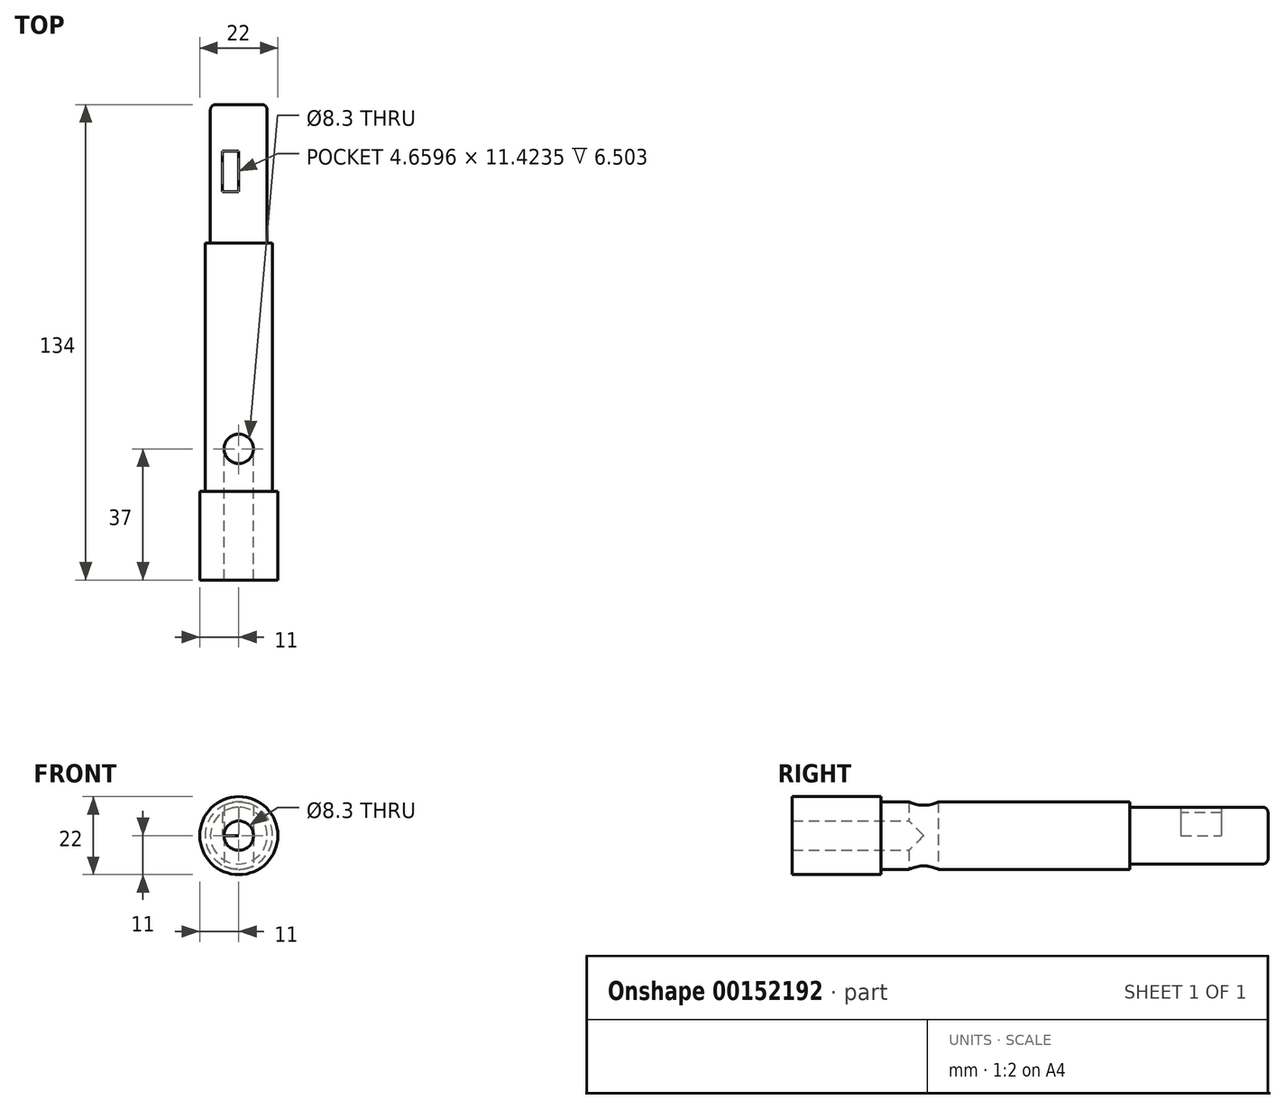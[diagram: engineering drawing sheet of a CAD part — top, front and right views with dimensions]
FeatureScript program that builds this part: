
annotation { "Feature Type Name" : "Feature", "Feature Type Description" : "" }
export const myFeature = defineFeature(function(context is Context, id is Id, definition is map)
    precondition{}
    {
        {
            var Q0;
            Q0=qCreatedBy(makeId("Front.planeOp"),FACE);
            var sketch = newSketch(context, id + "F0", { "sketchPlane" : qUnion([Q0])});
            skCircle(sketch, "E0", {"center": v(0, 0) * mm, "radius": 11 * mm});
            skCircle(sketch, "E1", {"center": v(0, 0) * mm, "radius": 4.15 * mm});
            skSolve(sketch);
        }
        {
            var Q0;
            Q0=makeQuery(id+"F0.imprint","IMPRINT",FACE,{"disambiguationData":[TD([[makeQuery(id+"F0.imprint","IMPRINT",EDGE,{"derivedFrom":sQuery(id+"F0.wireOp",EDGE,"E0")}),1.0]])]});
            extrude(context, id + "F1", {"entities" : qUnion([Q0]), "depth" : 25 * mm});
        }
        {
            var Q0;
            Q0=makeQuery(id+"F1.opExtrude","CAP_FACE",FACE,{"disambiguationData":[OSD([sQuery(id+"F0.wireOp",EDGE,"E0"),sQuery(id+"F0.wireOp",EDGE,"E1")])],"isStart":true});
            var sketch = newSketch(context, id + "F2", { "sketchPlane" : qUnion([Q0])});
            skCircle(sketch, "E2", {"center": v(0, 0) * mm, "radius": 9.5 * mm});
            skSolve(sketch);
        }
        {
            var Q0;
            Q0=makeQuery(id+"F2.imprint","IMPRINT",FACE,{"disambiguationData":[TD([[makeQuery(id+"F2.imprint","IMPRINT",EDGE,{"derivedFrom":sQuery(id+"F2.wireOp",EDGE,"E2")}),1.0]])]});
            var Q1;
            Q1=makeQuery(id+"F2.imprint","IMPRINT",FACE,{"disambiguationData":[TD([[makeQuery(id+"F2.imprint","IMPRINT",EDGE,{"derivedFrom":makeQuery(id+"F1.opExtrude","CAP_EDGE",EDGE,{"disambiguationData":[OSD([sQuery(id+"F0.wireOp",EDGE,"E1")])],"isStart":true})}),-1.0]])]});
            extrude(context, id + "F3", {"entities" : qUnion([Q0, Q1]), "operationType" : NewBodyOperationType.ADD, "depth" : 70 * mm});
        }
        {
            var Q0;
            Q0=qCreatedBy(makeId("Top.planeOp"),FACE);
            var sketch = newSketch(context, id + "F4", { "sketchPlane" : qUnion([Q0])});
            skLineSegment(sketch, "E3", {"start": v(0, 0) * mm, "end": v(0, 12) * mm, "construction": true});
            skCircle(sketch, "E4", {"center": v(0, 12) * mm, "radius": 4.15 * mm});
            skSolve(sketch);
        }
        {
            var Q0;
            Q0=qSketchRegion(id+"F4",true);
            extrude(context, id + "F5", {"entities" : qUnion([Q0]), "operationType" : NewBodyOperationType.REMOVE, "endBound" : BoundingType.THROUGH_ALL, "depth" : 25 * mm, "hasSecondDirection" : true, "secondDirectionOppositeDirection" : true, "secondDirectionDepth" : 25 * mm});
        }
        {
            var Q0;
            Q0=makeQuery(id+"F1.opExtrude","CAP_FACE",FACE,{"disambiguationData":[OSD([sQuery(id+"F0.wireOp",EDGE,"E0"),sQuery(id+"F0.wireOp",EDGE,"E1")])],"isStart":false});
            var sketch = newSketch(context, id + "F6", { "sketchPlane" : qUnion([Q0])});
            skCircle(sketch, "E5", {"center": v(0, 0) * mm, "radius": 4.15 * mm});
            skSolve(sketch);
        }
        {
            var Q0;
            Q0=makeQuery(id+"F6.imprint","IMPRINT",FACE,{"disambiguationData":[TD([[makeQuery(id+"F6.imprint","IMPRINT",EDGE,{"derivedFrom":sQuery(id+"F6.wireOp",EDGE,"E5")}),1.0]])]});
            extrude(context, id + "F7", {"entities" : qUnion([Q0]), "operationType" : NewBodyOperationType.REMOVE, "oppositeDirection" : true, "depth" : 37 * mm});
        }
        {
            var Q0;
            Q0=makeQuery(id+"F3.opExtrude","CAP_FACE",FACE,{"disambiguationData":[OSD([sQuery(id+"F2.wireOp",EDGE,"E2")])],"isStart":false});
            var sketch = newSketch(context, id + "F8", { "sketchPlane" : qUnion([Q0])});
            skCircle(sketch, "E6", {"center": v(0, 0) * mm, "radius": 8 * mm});
            skSolve(sketch);
        }
        {
            var Q0;
            Q0=makeQuery(id+"F8.imprint","IMPRINT",FACE,{"disambiguationData":[TD([[makeQuery(id+"F8.imprint","IMPRINT",EDGE,{"derivedFrom":sQuery(id+"F8.wireOp",EDGE,"E6")}),1.0]])]});
            extrude(context, id + "F9", {"entities" : qUnion([Q0]), "operationType" : NewBodyOperationType.ADD, "depth" : 39 * mm});
        }
        {
            var Q0;
            Q0=makeQuery(id+"F9.opExtrude","CAP_EDGE",EDGE,{"disambiguationData":[OSD([sQuery(id+"F8.wireOp",EDGE,"E6")])],"isStart":false});
            fillet(context, id + "F10", {"entities" : qUnion([Q0]), "radius" : 1.5 * mm, "tangentPropagation" : true, "allowEdgeOverflow" : false});
        }
        {
            var Q0;
            Q0=qCreatedBy(makeId("Top.planeOp"),FACE);
            var sketch = newSketch(context, id + "F11", { "sketchPlane" : qUnion([Q0])});
            skLineSegment(sketch, "E7.bottom", {"start": v(0, 84.47) * mm, "end": v(-4.66, 84.47) * mm});
            skLineSegment(sketch, "E7.top", {"start": v(0, 95.9) * mm, "end": v(-4.66, 95.9) * mm});
            skLineSegment(sketch, "E7.left", {"start": v(0, 84.47) * mm, "end": v(0, 95.9) * mm});
            skLineSegment(sketch, "E7.right", {"start": v(-4.66, 84.47) * mm, "end": v(-4.66, 95.9) * mm});
            skSolve(sketch);
        }
        {
            var Q0;
            Q0=qSketchRegion(id+"F11",true);
            extrude(context, id + "F12", {"entities" : qUnion([Q0]), "operationType" : NewBodyOperationType.REMOVE, "depth" : 25 * mm});
        }
    });
